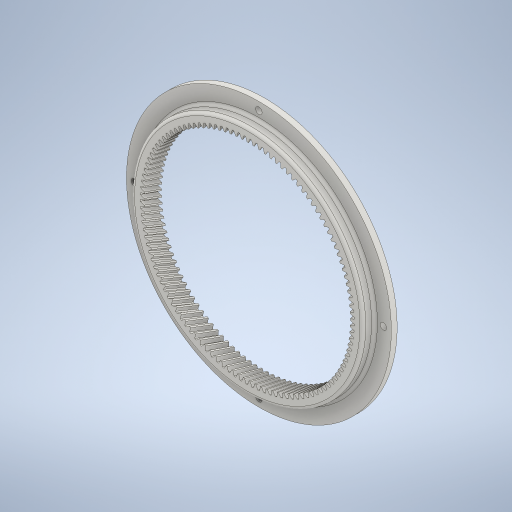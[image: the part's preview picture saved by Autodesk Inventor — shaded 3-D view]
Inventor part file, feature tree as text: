
AUTODESK INVENTOR PART (.ipt)
format: ipt  version: 2024 (Build 280153000, 153)  size: 1,564,672 bytes
history: native  units: mm (DEFAULTED — no unit token found)
features: plane x3, other x3, sketch x3, extrude x2, hole x1, fillet x1
ambient origin geometry x8: Origin, YZ Plane, XZ Plane, XY Plane, X Axis, Y Axis, Z Axis, Center Point
bodies: Solid1 (feature_tree)
feature tree (13):
  extrude  "Extrusion1"  Depth=15.0mm TaperAngle=0.0deg
  plane  "Work Plane2"
  plane  "Work Plane8"
  plane  "Work Plane9"
  other  "Spur Gear"
  extrude  "Extrusion2"  Depth=10.0mm TaperAngle=0.0deg
  hole  "Hole3"  [1 undecoded]
  fillet  "Fillet1"  [1 undecoded]
  sketch  "Sketch1"  dims[d0=198.985007mm d1=15.0mm d2=0.0mm]
  other  "Srf1"
  sketch  "Sketch3"  dims[d3=180.378132mm d4=10.0mm d5=0.0mm]
  sketch  "Sketch6"  dims[d16=63.909111mm d17=0.0mm d34=0.278017mm d39=0.0mm d45=0.0mm d47=63.909111mm d50=0.0mm d51=0.0mm d52=63.909111mm d53=5.0mm d54=0.0mm d69=5.5mm d70=6.0mm d71=4.0mm d72=2.0mm d73=90.0deg d74=8.0mm d75=20.594885mm d76=214.257426mm d77=214.257426mm d78=107.128713mm d79=107.128713mm d80=2.5mm d81=228.0mm]
  other  "Pitch Diameter"
note: 2 required parameter values undecoded (feature->parameter linkage not recoverable at this tier; creation-order binding heuristic only, values carry confidence <= 0.55)
